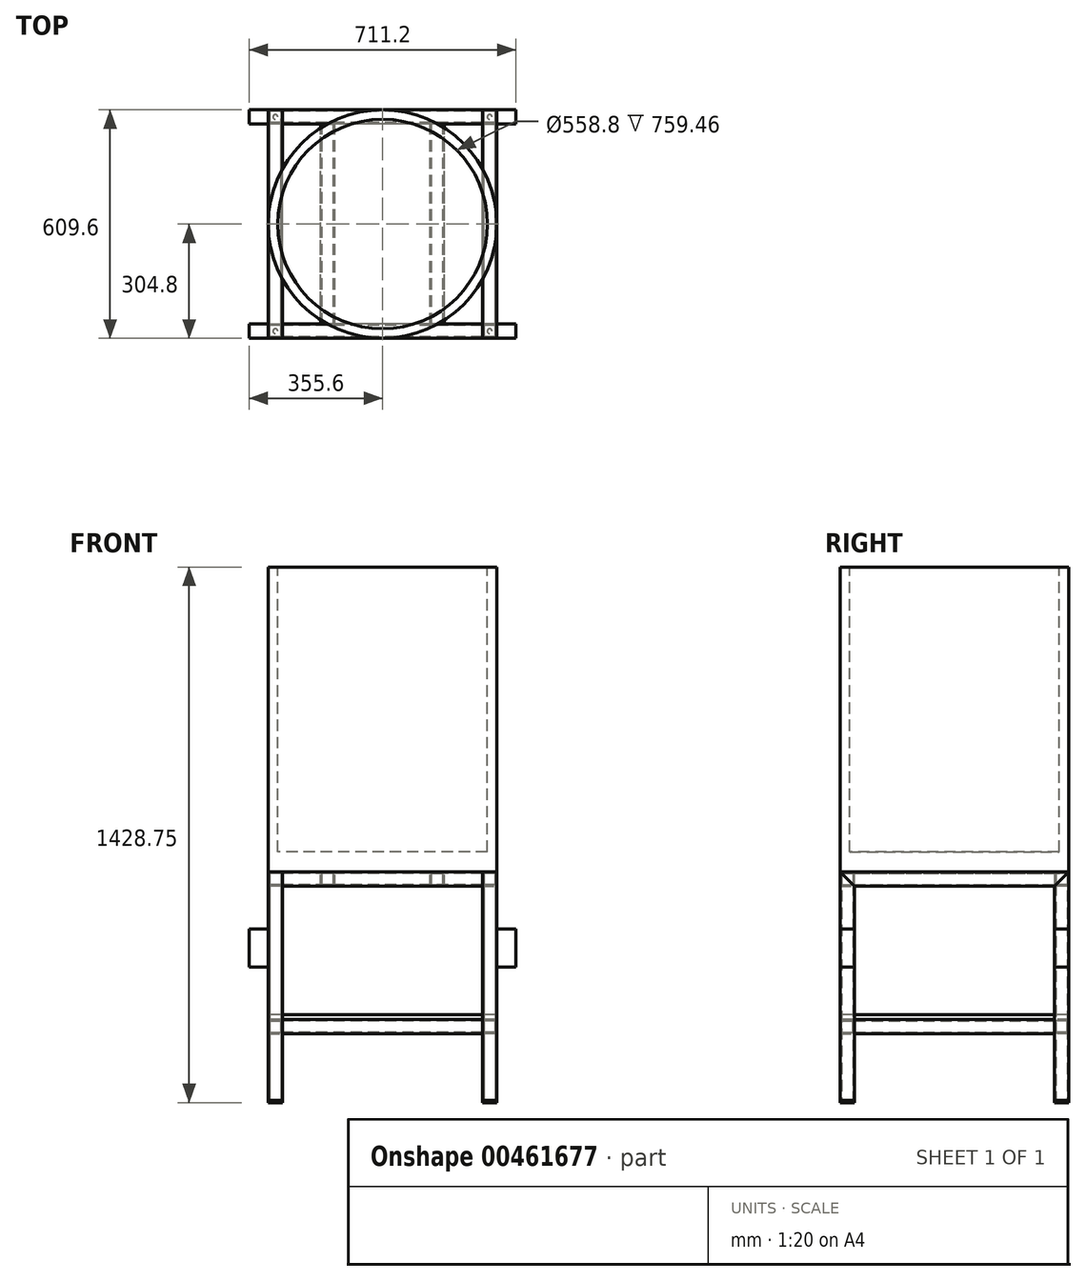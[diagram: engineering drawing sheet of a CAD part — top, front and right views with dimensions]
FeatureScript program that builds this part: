
annotation { "Feature Type Name" : "Feature", "Feature Type Description" : "" }
export const myFeature = defineFeature(function(context is Context, id is Id, definition is map)
    precondition{}
    {
        {
            var Q0;
            Q0=qCreatedBy(makeId("Top.planeOp"),FACE);
            var sketch = newSketch(context, id + "F0", { "sketchPlane" : qUnion([Q0])});
            skCircle(sketch, "E0", {"center": v(0, 0) * mm, "radius": 304.8 * mm});
            skSolve(sketch);
        }
        {
            var Q0;
            Q0=makeQuery(id+"F0.imprint","IMPRINT",FACE,{"disambiguationData":[TD([[makeQuery(id+"F0.imprint","IMPRINT",EDGE,{"derivedFrom":sQuery(id+"F0.wireOp",EDGE,"E0")}),1.0]])]});
            extrude(context, id + "F1", {"entities" : qUnion([Q0]), "depth" : 812.8 * mm});
        }
        {
            var Q0;
            Q0=qCreatedBy(makeId("Front.planeOp"),FACE);
            var sketch = newSketch(context, id + "F2", { "sketchPlane" : qUnion([Q0])});
            skLineSegment(sketch, "E1.bottom", {"start": v(304.8, -38.1) * mm, "end": v(266.7, -38.1) * mm});
            skLineSegment(sketch, "E1.top", {"start": v(304.8, 0) * mm, "end": v(266.7, 0) * mm});
            skLineSegment(sketch, "E1.left", {"start": v(304.8, -38.1) * mm, "end": v(304.8, 0) * mm});
            skLineSegment(sketch, "E1.right", {"start": v(266.7, -38.1) * mm, "end": v(266.7, 0) * mm});
            skPoint(sketch, "E1.middle", {"position": v(285.75, -19.05) * mm});
            skLineSegment(sketch, "E2.0", {"start": v(301, -3.81) * mm, "end": v(270.5, -3.81) * mm});
            skLineSegment(sketch, "E2.1", {"start": v(301, -34.3) * mm, "end": v(301, -3.81) * mm});
            skLineSegment(sketch, "E2.2", {"start": v(301, -34.3) * mm, "end": v(270.5, -34.3) * mm});
            skLineSegment(sketch, "E2.3", {"start": v(270.5, -34.3) * mm, "end": v(270.5, -3.81) * mm});
            skSolve(sketch);
        }
        {
            var Q0;
            Q0 = qSketchRegion(id + "F2", true);
            extrude(context, id + "F3", {"entities" : qUnion([Q0]), "endBound" : BoundingType.SYMMETRIC, "depth" : 609.6 * mm});
        }
        {
            var Q0;
            Q0=makeQuery(id+"F3.opExtrude","SWEPT_FACE",FACE,{"disambiguationData":[OSD([sQuery(id+"F2.wireOp",EDGE,"E1.left")])]});
            var sketch = newSketch(context, id + "F4", { "sketchPlane" : qUnion([Q0])});
            skLineSegment(sketch, "E3", {"start": v(-304.8, 0) * mm, "end": v(-266.7, -38.1) * mm});
            skLineSegment(sketch, "E4", {"start": v(-266.7, -38.1) * mm, "end": v(-266.7, -51.91) * mm});
            skLineSegment(sketch, "E5", {"start": v(-266.7, -51.91) * mm, "end": v(-315.93, -51.91) * mm});
            skLineSegment(sketch, "E6", {"start": v(-315.93, -51.91) * mm, "end": v(-315.93, 0) * mm});
            skLineSegment(sketch, "E7", {"start": v(-315.93, 0) * mm, "end": v(-304.8, 0) * mm});
            skLineSegment(sketch, "E8", {"start": v(0, 0) * mm, "end": v(0, -21.94) * mm, "construction": true});
            skLineSegment(sketch, "E9.MirrorCS", {"start": v(315.93, 0) * mm, "end": v(304.8, 0) * mm});
            skLineSegment(sketch, "E10.MirrorCS", {"start": v(266.7, -38.1) * mm, "end": v(266.7, -51.91) * mm});
            skLineSegment(sketch, "E11.MirrorCS", {"start": v(304.8, 0) * mm, "end": v(266.7, -38.1) * mm});
            skLineSegment(sketch, "E12.MirrorCS", {"start": v(266.7, -51.91) * mm, "end": v(315.93, -51.91) * mm});
            skLineSegment(sketch, "E13.MirrorCS", {"start": v(315.93, -51.91) * mm, "end": v(315.93, 0) * mm});
            skSolve(sketch);
        }
        {
            var Q0;
            Q0 = qSketchRegion(id + "F4", true);
            var Q1;
            Q1=makeQuery(id+"F3.opExtrude","SWEPT_FACE",FACE,{"disambiguationData":[OSD([sQuery(id+"F2.wireOp",EDGE,"E1.right")])]});
            extrude(context, id + "F5", {"entities" : qUnion([Q0]), "operationType" : NewBodyOperationType.REMOVE, "endBound" : BoundingType.UP_TO_SURFACE, "oppositeDirection" : true, "endBoundEntityFace" : qUnion([Q1]), "depth" : 25.4 * mm});
        }
        {
            var Q0;
            Q0=makeQuery(id+"F3.opExtrude","SWEPT_BODY",BODY,{"disambiguationData":[OSD([sQuery(id+"F2.wireOp",EDGE,"E1.bottom"),sQuery(id+"F2.wireOp",EDGE,"E1.top"),sQuery(id+"F2.wireOp",EDGE,"E1.left"),sQuery(id+"F2.wireOp",EDGE,"E1.right"),sQuery(id+"F2.wireOp",EDGE,"E2.0"),sQuery(id+"F2.wireOp",EDGE,"E2.1"),sQuery(id+"F2.wireOp",EDGE,"E2.2"),sQuery(id+"F2.wireOp",EDGE,"E2.3")])]});
            var Q1;
            Q1=qCreatedBy(makeId("Right.planeOp"),FACE);
            mirror(context, id + "F6", {"entities" : qUnion([Q0]), "mirrorPlane" : qUnion([Q1])});
        }
        {
            var Q0;
            Q0=qCreatedBy(makeId("Top.planeOp"),FACE);
            cPlane(context, id + "F7", {"entities" : qUnion([Q0]), "cplaneType" : CPlaneType.OFFSET, "offset" : 609.6 * mm, "oppositeDirection" : true, "width" : 152.4 * mm, "height" : 152.4 * mm});
        }
        {
            var Q0;
            Q0=qCreatedBy(id+"F7.planeOp",FACE);
            var sketch = newSketch(context, id + "F8", { "sketchPlane" : qUnion([Q0])});
            skLineSegment(sketch, "E14.bottom", {"start": v(304.8, -266.7) * mm, "end": v(266.7, -266.7) * mm});
            skLineSegment(sketch, "E14.top", {"start": v(304.8, -304.8) * mm, "end": v(266.7, -304.8) * mm});
            skLineSegment(sketch, "E14.left", {"start": v(304.8, -266.7) * mm, "end": v(304.8, -304.8) * mm});
            skLineSegment(sketch, "E14.right", {"start": v(266.7, -266.7) * mm, "end": v(266.7, -304.8) * mm});
            skPoint(sketch, "E14.middle", {"position": v(285.75, -285.75) * mm});
            skLineSegment(sketch, "E15.0", {"start": v(270.5, -270.51) * mm, "end": v(270.5, -301) * mm});
            skLineSegment(sketch, "E15.1", {"start": v(300.99, -270.51) * mm, "end": v(270.5, -270.51) * mm});
            skLineSegment(sketch, "E15.2", {"start": v(300.99, -270.51) * mm, "end": v(300.99, -301) * mm});
            skLineSegment(sketch, "E15.3", {"start": v(300.99, -301) * mm, "end": v(270.5, -301) * mm});
            skSolve(sketch);
        }
        {
            var Q0;
            Q0 = qSketchRegion(id + "F8", true);
            var Q1;
            Q1=makeQuery(id+"F5.boolean.opBoolean","COPY",FACE,{"derivedFrom":makeQuery(id+"F5.opExtrude","SWEPT_FACE",FACE,{"disambiguationData":[OSD([sQuery(id+"F4.wireOp",EDGE,"E3")])]})});
            extrude(context, id + "F9", {"entities" : qUnion([Q0]), "endBound" : BoundingType.UP_TO_SURFACE, "endBoundEntityFace" : qUnion([Q1]), "depth" : 345.44 * mm});
        }
        {
            var Q0;
            Q0=makeQuery(id+"F9.opExtrude","SWEPT_BODY",BODY,{"disambiguationData":[OSD([sQuery(id+"F8.wireOp",EDGE,"E14.bottom"),sQuery(id+"F8.wireOp",EDGE,"E14.top"),sQuery(id+"F8.wireOp",EDGE,"E14.left"),sQuery(id+"F8.wireOp",EDGE,"E14.right"),sQuery(id+"F8.wireOp",EDGE,"E15.0"),sQuery(id+"F8.wireOp",EDGE,"E15.1"),sQuery(id+"F8.wireOp",EDGE,"E15.2"),sQuery(id+"F8.wireOp",EDGE,"E15.3")])]});
            var Q1;
            Q1=qCreatedBy(makeId("Front.planeOp"),FACE);
            mirror(context, id + "F10", {"entities" : qUnion([Q0]), "mirrorPlane" : qUnion([Q1])});
        }
        {
            var Q0;
            Q0=makeQuery(id+"F9.opExtrude","SWEPT_BODY",BODY,{"disambiguationData":[OSD([sQuery(id+"F8.wireOp",EDGE,"E14.bottom"),sQuery(id+"F8.wireOp",EDGE,"E14.top"),sQuery(id+"F8.wireOp",EDGE,"E14.left"),sQuery(id+"F8.wireOp",EDGE,"E14.right"),sQuery(id+"F8.wireOp",EDGE,"E15.0"),sQuery(id+"F8.wireOp",EDGE,"E15.1"),sQuery(id+"F8.wireOp",EDGE,"E15.2"),sQuery(id+"F8.wireOp",EDGE,"E15.3")])]});
            var Q1;
            Q1=makeQuery(id+"F10.opPattern","COPY",BODY,{"derivedFrom":makeQuery(id+"F9.opExtrude","SWEPT_BODY",BODY,{"disambiguationData":[OSD([sQuery(id+"F8.wireOp",EDGE,"E14.bottom"),sQuery(id+"F8.wireOp",EDGE,"E14.top"),sQuery(id+"F8.wireOp",EDGE,"E14.left"),sQuery(id+"F8.wireOp",EDGE,"E14.right"),sQuery(id+"F8.wireOp",EDGE,"E15.0"),sQuery(id+"F8.wireOp",EDGE,"E15.1"),sQuery(id+"F8.wireOp",EDGE,"E15.2"),sQuery(id+"F8.wireOp",EDGE,"E15.3")])]}),"instanceName":"1"});
            var Q2;
            Q2=qCreatedBy(makeId("Right.planeOp"),FACE);
            mirror(context, id + "F11", {"entities" : qUnion([Q0, Q1]), "mirrorPlane" : qUnion([Q2])});
        }
        {
            var Q0;
            Q0=qCreatedBy(makeId("Right.planeOp"),FACE);
            var sketch = newSketch(context, id + "F12", { "sketchPlane" : qUnion([Q0])});
            skLineSegment(sketch, "E16.bottom", {"start": v(-266.7, -38.1) * mm, "end": v(-304.8, -38.1) * mm});
            skLineSegment(sketch, "E16.top", {"start": v(-266.7, 0) * mm, "end": v(-304.8, 0) * mm});
            skLineSegment(sketch, "E16.left", {"start": v(-266.7, -38.1) * mm, "end": v(-266.7, 0) * mm});
            skLineSegment(sketch, "E16.right", {"start": v(-304.8, -38.1) * mm, "end": v(-304.8, 0) * mm});
            skPoint(sketch, "E16.middle", {"position": v(-285.75, -19.05) * mm});
            skLineSegment(sketch, "E17.0", {"start": v(-270.51, -3.81) * mm, "end": v(-301, -3.81) * mm});
            skLineSegment(sketch, "E17.1", {"start": v(-270.51, -34.29) * mm, "end": v(-270.51, -3.81) * mm});
            skLineSegment(sketch, "E17.2", {"start": v(-270.51, -34.29) * mm, "end": v(-301, -34.29) * mm});
            skLineSegment(sketch, "E17.3", {"start": v(-301, -34.29) * mm, "end": v(-301, -3.81) * mm});
            skSolve(sketch);
        }
        {
            var Q0;
            Q0 = qSketchRegion(id + "F12", true);
            var Q1;
            Q1=makeQuery(id+"F3.opExtrude","SWEPT_FACE",FACE,{"disambiguationData":[OSD([sQuery(id+"F2.wireOp",EDGE,"E1.right")])]});
            var Q2;
            Q2=makeQuery(id+"F6.opPattern","COPY",FACE,{"derivedFrom":makeQuery(id+"F3.opExtrude","SWEPT_FACE",FACE,{"disambiguationData":[OSD([sQuery(id+"F2.wireOp",EDGE,"E1.right")])]}),"instanceName":"1"});
            extrude(context, id + "F13", {"entities" : qUnion([Q0]), "endBound" : BoundingType.UP_TO_SURFACE, "endBoundEntityFace" : qUnion([Q1]), "depth" : 533.4 * mm, "hasSecondDirection" : true, "secondDirectionBound" : SecondDirectionBoundingType.UP_TO_SURFACE, "secondDirectionOppositeDirection" : true, "secondDirectionBoundEntityFace" : qUnion([Q2]), "secondDirectionDepth" : 25.4 * mm});
        }
        {
            var Q0;
            Q0=makeQuery(id+"F13.opExtrude","SWEPT_BODY",BODY,{"disambiguationData":[OSD([sQuery(id+"F12.wireOp",EDGE,"E16.bottom"),sQuery(id+"F12.wireOp",EDGE,"E16.top"),sQuery(id+"F12.wireOp",EDGE,"E16.left"),sQuery(id+"F12.wireOp",EDGE,"E16.right"),sQuery(id+"F12.wireOp",EDGE,"E17.0"),sQuery(id+"F12.wireOp",EDGE,"E17.1"),sQuery(id+"F12.wireOp",EDGE,"E17.2"),sQuery(id+"F12.wireOp",EDGE,"E17.3")])]});
            var Q1;
            Q1=qCreatedBy(makeId("Front.planeOp"),FACE);
            mirror(context, id + "F14", {"entities" : qUnion([Q0]), "mirrorPlane" : qUnion([Q1])});
        }
        {
            var Q0;
            Q0=makeQuery(id+"F13.opExtrude","SWEPT_FACE",FACE,{"disambiguationData":[OSD([sQuery(id+"F12.wireOp",EDGE,"E16.bottom")])]});
            cPlane(context, id + "F15", {"entities" : qUnion([Q0]), "cplaneType" : CPlaneType.OFFSET, "offset" : 177.8 * mm, "width" : 152.4 * mm, "height" : 152.4 * mm});
        }
        {
            var Q0;
            Q0=makeQuery(id+"F13.opExtrude","SWEPT_BODY",BODY,{"disambiguationData":[OSD([sQuery(id+"F12.wireOp",EDGE,"E16.bottom"),sQuery(id+"F12.wireOp",EDGE,"E16.top"),sQuery(id+"F12.wireOp",EDGE,"E16.left"),sQuery(id+"F12.wireOp",EDGE,"E16.right"),sQuery(id+"F12.wireOp",EDGE,"E17.0"),sQuery(id+"F12.wireOp",EDGE,"E17.1"),sQuery(id+"F12.wireOp",EDGE,"E17.2"),sQuery(id+"F12.wireOp",EDGE,"E17.3")])]});
            var Q1;
            Q1=makeQuery(id+"F14.opPattern","COPY",BODY,{"derivedFrom":makeQuery(id+"F13.opExtrude","SWEPT_BODY",BODY,{"disambiguationData":[OSD([sQuery(id+"F12.wireOp",EDGE,"E16.bottom"),sQuery(id+"F12.wireOp",EDGE,"E16.top"),sQuery(id+"F12.wireOp",EDGE,"E16.left"),sQuery(id+"F12.wireOp",EDGE,"E16.right"),sQuery(id+"F12.wireOp",EDGE,"E17.0"),sQuery(id+"F12.wireOp",EDGE,"E17.1"),sQuery(id+"F12.wireOp",EDGE,"E17.2"),sQuery(id+"F12.wireOp",EDGE,"E17.3")])]}),"instanceName":"1"});
            var Q2;
            Q2=qCreatedBy(id+"F15.planeOp",FACE);
            mirror(context, id + "F16", {"entities" : qUnion([Q0, Q1]), "mirrorPlane" : qUnion([Q2])});
        }
        {
            var Q0;
            Q0=qCreatedBy(makeId("Front.planeOp"),FACE);
            var sketch = newSketch(context, id + "F17", { "sketchPlane" : qUnion([Q0])});
            skLineSegment(sketch, "E18.bottom", {"start": v(304.8, -431.8) * mm, "end": v(266.7, -431.8) * mm});
            skLineSegment(sketch, "E18.top", {"start": v(304.8, -393.7) * mm, "end": v(266.7, -393.7) * mm});
            skLineSegment(sketch, "E18.left", {"start": v(304.8, -431.8) * mm, "end": v(304.8, -393.7) * mm});
            skLineSegment(sketch, "E18.right", {"start": v(266.7, -431.8) * mm, "end": v(266.7, -393.7) * mm});
            skPoint(sketch, "E18.middle", {"position": v(285.75, -412.75) * mm});
            skLineSegment(sketch, "E19.0", {"start": v(300.99, -397.5) * mm, "end": v(270.5, -397.5) * mm});
            skLineSegment(sketch, "E19.1", {"start": v(300.99, -427.99) * mm, "end": v(300.99, -397.5) * mm});
            skLineSegment(sketch, "E19.2", {"start": v(300.99, -427.99) * mm, "end": v(270.5, -427.99) * mm});
            skLineSegment(sketch, "E19.3", {"start": v(270.5, -427.99) * mm, "end": v(270.5, -397.5) * mm});
            skSolve(sketch);
        }
        {
            var Q0;
            Q0 = qSketchRegion(id + "F17", true);
            extrude(context, id + "F18", {"entities" : qUnion([Q0]), "endBound" : BoundingType.UP_TO_NEXT, "depth" : 25.4 * mm, "hasSecondDirection" : true, "secondDirectionBound" : SecondDirectionBoundingType.UP_TO_NEXT, "secondDirectionOppositeDirection" : true, "secondDirectionDepth" : 25.4 * mm});
        }
        {
            var Q0;
            Q0=makeQuery(id+"F18.opExtrude","SWEPT_BODY",BODY,{"disambiguationData":[OSD([sQuery(id+"F17.wireOp",EDGE,"E18.bottom"),sQuery(id+"F17.wireOp",EDGE,"E18.top"),sQuery(id+"F17.wireOp",EDGE,"E18.left"),sQuery(id+"F17.wireOp",EDGE,"E18.right"),sQuery(id+"F17.wireOp",EDGE,"E19.0"),sQuery(id+"F17.wireOp",EDGE,"E19.1"),sQuery(id+"F17.wireOp",EDGE,"E19.2"),sQuery(id+"F17.wireOp",EDGE,"E19.3")])]});
            var Q1;
            Q1=qCreatedBy(makeId("Right.planeOp"),FACE);
            mirror(context, id + "F19", {"entities" : qUnion([Q0]), "mirrorPlane" : qUnion([Q1])});
        }
        {
            var Q0;
            Q0=qCreatedBy(makeId("Front.planeOp"),FACE);
            var sketch = newSketch(context, id + "F20", { "sketchPlane" : qUnion([Q0])});
            skLineSegment(sketch, "E20.bottom", {"start": v(-127, -38.1) * mm, "end": v(-165.1, -38.1) * mm});
            skLineSegment(sketch, "E20.top", {"start": v(-127, 0) * mm, "end": v(-165.1, 0) * mm});
            skLineSegment(sketch, "E20.left", {"start": v(-127, -38.1) * mm, "end": v(-127, 0) * mm});
            skLineSegment(sketch, "E20.right", {"start": v(-165.1, -38.1) * mm, "end": v(-165.1, 0) * mm});
            skPoint(sketch, "E20.middle", {"position": v(-146.05, -19.05) * mm});
            skLineSegment(sketch, "E21.0", {"start": v(-130.81, -3.8) * mm, "end": v(-161.29, -3.81) * mm});
            skLineSegment(sketch, "E21.1", {"start": v(-130.81, -34.29) * mm, "end": v(-130.81, -3.8) * mm});
            skLineSegment(sketch, "E21.2", {"start": v(-130.81, -34.29) * mm, "end": v(-161.29, -34.29) * mm});
            skLineSegment(sketch, "E21.3", {"start": v(-161.29, -34.29) * mm, "end": v(-161.29, -3.81) * mm});
            skSolve(sketch);
        }
        {
            var Q0;
            Q0 = qSketchRegion(id + "F20", true);
            extrude(context, id + "F21", {"entities" : qUnion([Q0]), "endBound" : BoundingType.UP_TO_NEXT, "depth" : 25.4 * mm, "hasSecondDirection" : true, "secondDirectionBound" : SecondDirectionBoundingType.UP_TO_NEXT, "secondDirectionOppositeDirection" : true, "secondDirectionDepth" : 25.4 * mm});
        }
        {
            var Q0;
            Q0=makeQuery(id+"F21.opExtrude","SWEPT_BODY",BODY,{"disambiguationData":[OSD([sQuery(id+"F20.wireOp",EDGE,"E20.bottom"),sQuery(id+"F20.wireOp",EDGE,"E20.top"),sQuery(id+"F20.wireOp",EDGE,"E20.left"),sQuery(id+"F20.wireOp",EDGE,"E20.right"),sQuery(id+"F20.wireOp",EDGE,"E21.0"),sQuery(id+"F20.wireOp",EDGE,"E21.1"),sQuery(id+"F20.wireOp",EDGE,"E21.2"),sQuery(id+"F20.wireOp",EDGE,"E21.3")])]});
            var Q1;
            Q1=qCreatedBy(makeId("Right.planeOp"),FACE);
            mirror(context, id + "F22", {"entities" : qUnion([Q0]), "mirrorPlane" : qUnion([Q1])});
        }
        {
            var Q0;
            Q0=makeQuery(id+"F19.opPattern","COPY",FACE,{"derivedFrom":makeQuery(id+"F18.opExtrude","SWEPT_FACE",FACE,{"disambiguationData":[OSD([sQuery(id+"F17.wireOp",EDGE,"E18.top")])]}),"instanceName":"1"});
            var sketch = newSketch(context, id + "F23", { "sketchPlane" : qUnion([Q0])});
            skLineSegment(sketch, "E22.0", {"start": v(266.7, -304.8) * mm, "end": v(-266.7, -304.8) * mm});
            skLineSegment(sketch, "E23.0", {"start": v(266.7, 304.8) * mm, "end": v(-266.7, 304.8) * mm});
            skLineSegment(sketch, "E24", {"start": v(-266.7, 304.8) * mm, "end": v(-266.7, 266.7) * mm});
            skLineSegment(sketch, "E25", {"start": v(-266.7, 266.7) * mm, "end": v(-304.8, 266.7) * mm});
            skLineSegment(sketch, "E26", {"start": v(-304.8, 266.7) * mm, "end": v(-304.8, -266.7) * mm});
            skLineSegment(sketch, "E27", {"start": v(-304.8, -266.7) * mm, "end": v(-266.7, -266.7) * mm});
            skLineSegment(sketch, "E28", {"start": v(-266.7, -266.7) * mm, "end": v(-266.7, -304.8) * mm});
            skLineSegment(sketch, "E29", {"start": v(0, 0) * mm, "end": v(0, 69.38) * mm, "construction": true});
            skLineSegment(sketch, "E30", {"start": v(0, 0) * mm, "end": v(64.68, 0) * mm, "construction": true});
            skLineSegment(sketch, "E31.MirrorCS", {"start": v(304.8, 266.7) * mm, "end": v(304.8, -266.7) * mm});
            skLineSegment(sketch, "E32.MirrorCS", {"start": v(266.7, 266.7) * mm, "end": v(304.8, 266.7) * mm});
            skLineSegment(sketch, "E33.MirrorCS", {"start": v(304.8, -266.7) * mm, "end": v(266.7, -266.7) * mm});
            skLineSegment(sketch, "E34", {"start": v(266.7, -304.8) * mm, "end": v(266.7, -266.7) * mm});
            skLineSegment(sketch, "E35", {"start": v(266.7, 304.8) * mm, "end": v(266.7, 266.7) * mm});
            skSolve(sketch);
        }
        {
            var Q0;
            Q0 = qSketchRegion(id + "F23", true);
            extrude(context, id + "F24", {"entities" : qUnion([Q0]), "depth" : 12.7 * mm});
        }
        {
            var Q0;
            Q0=qCreatedBy(id+"F7.planeOp",FACE);
            var sketch = newSketch(context, id + "F25", { "sketchPlane" : qUnion([Q0])});
            skLineSegment(sketch, "E36.bottom", {"start": v(304.8, -304.8) * mm, "end": v(266.7, -304.8) * mm});
            skLineSegment(sketch, "E36.top", {"start": v(304.8, -266.7) * mm, "end": v(266.7, -266.7) * mm});
            skLineSegment(sketch, "E36.left", {"start": v(304.8, -304.8) * mm, "end": v(304.8, -266.7) * mm});
            skLineSegment(sketch, "E36.right", {"start": v(266.7, -304.8) * mm, "end": v(266.7, -266.7) * mm});
            skLineSegment(sketch, "E37", {"start": v(266.7, -304.8) * mm, "end": v(304.8, -266.7) * mm, "construction": true});
            skLineSegment(sketch, "E38", {"start": v(304.8, -304.8) * mm, "end": v(266.7, -266.7) * mm, "construction": true});
            skCircle(sketch, "E39", {"center": v(285.75, -285.75) * mm, "radius": 6.35 * mm});
            skSolve(sketch);
        }
        {
            var Q0;
            Q0 = qSketchRegion(id + "F25", true);
            extrude(context, id + "F26", {"entities" : qUnion([Q0]), "oppositeDirection" : true, "depth" : 6.35 * mm});
        }
        {
            var Q0;
            Q0=makeQuery(id+"F26.opExtrude","SWEPT_BODY",BODY,{"disambiguationData":[OSD([sQuery(id+"F25.wireOp",EDGE,"E36.bottom"),sQuery(id+"F25.wireOp",EDGE,"E36.top"),sQuery(id+"F25.wireOp",EDGE,"E36.left"),sQuery(id+"F25.wireOp",EDGE,"E36.right"),sQuery(id+"F25.wireOp",EDGE,"E39")])]});
            var Q1;
            Q1=qCreatedBy(makeId("Right.planeOp"),FACE);
            mirror(context, id + "F27", {"entities" : qUnion([Q0]), "mirrorPlane" : qUnion([Q1])});
        }
        {
            var Q0;
            Q0=makeQuery(id+"F26.opExtrude","SWEPT_BODY",BODY,{"disambiguationData":[OSD([sQuery(id+"F25.wireOp",EDGE,"E36.bottom"),sQuery(id+"F25.wireOp",EDGE,"E36.top"),sQuery(id+"F25.wireOp",EDGE,"E36.left"),sQuery(id+"F25.wireOp",EDGE,"E36.right"),sQuery(id+"F25.wireOp",EDGE,"E39")])]});
            var Q1;
            Q1=makeQuery(id+"F27.opPattern","COPY",BODY,{"derivedFrom":makeQuery(id+"F26.opExtrude","SWEPT_BODY",BODY,{"disambiguationData":[OSD([sQuery(id+"F25.wireOp",EDGE,"E36.bottom"),sQuery(id+"F25.wireOp",EDGE,"E36.top"),sQuery(id+"F25.wireOp",EDGE,"E36.left"),sQuery(id+"F25.wireOp",EDGE,"E36.right"),sQuery(id+"F25.wireOp",EDGE,"E39")])]}),"instanceName":"1"});
            var Q2;
            Q2=qCreatedBy(makeId("Front.planeOp"),FACE);
            mirror(context, id + "F28", {"entities" : qUnion([Q0, Q1]), "mirrorPlane" : qUnion([Q2])});
        }
        {
            var Q0;
            Q0=makeQuery(id+"F1.opExtrude","CAP_FACE",FACE,{"disambiguationData":[OSD([sQuery(id+"F0.wireOp",EDGE,"E0")])],"isStart":false});
            var sketch = newSketch(context, id + "F29", { "sketchPlane" : qUnion([Q0])});
            skCircle(sketch, "E40", {"center": v(0, 0) * mm, "radius": 279.4 * mm});
            skSolve(sketch);
        }
        {
            var Q0;
            Q0 = qSketchRegion(id + "F29", true);
            extrude(context, id + "F30", {"entities" : qUnion([Q0]), "operationType" : NewBodyOperationType.REMOVE, "oppositeDirection" : true, "depth" : 759.46 * mm});
        }
        {
            var Q0;
            Q0=makeQuery(id+"F11.opPattern","COPY",FACE,{"derivedFrom":makeQuery(id+"F9.opExtrude","SWEPT_FACE",FACE,{"disambiguationData":[OSD([sQuery(id+"F8.wireOp",EDGE,"E14.left")])]}),"instanceName":"1"});
            var sketch = newSketch(context, id + "F31", { "sketchPlane" : qUnion([Q0])});
            skLineSegment(sketch, "E41.bottom", {"start": v(-304.8, -152.4) * mm, "end": v(-266.7, -152.4) * mm});
            skLineSegment(sketch, "E41.top", {"start": v(-304.8, -254) * mm, "end": v(-266.7, -254) * mm});
            skLineSegment(sketch, "E41.left", {"start": v(-304.8, -152.4) * mm, "end": v(-304.8, -254) * mm});
            skLineSegment(sketch, "E41.right", {"start": v(-266.7, -152.4) * mm, "end": v(-266.7, -254) * mm});
            skLineSegment(sketch, "E42", {"start": v(0, 0) * mm, "end": v(0, -69.92) * mm, "construction": true});
            skLineSegment(sketch, "E43.MirrorCS", {"start": v(304.8, -254) * mm, "end": v(266.7, -254) * mm});
            skLineSegment(sketch, "E44.MirrorCS", {"start": v(304.8, -152.4) * mm, "end": v(266.7, -152.4) * mm});
            skLineSegment(sketch, "E45.MirrorCS", {"start": v(266.7, -152.4) * mm, "end": v(266.7, -254) * mm});
            skLineSegment(sketch, "E46.MirrorCS", {"start": v(304.8, -152.4) * mm, "end": v(304.8, -254) * mm});
            skSolve(sketch);
        }
        {
            var Q0;
            Q0 = qSketchRegion(id + "F31", true);
            extrude(context, id + "F32", {"entities" : qUnion([Q0]), "depth" : 50.8 * mm});
        }
        {
            var Q0;
            Q0=makeQuery(id+"F32.opExtrude","SWEPT_BODY",BODY,{"disambiguationData":[OSD([sQuery(id+"F31.wireOp",EDGE,"E43.MirrorCS"),sQuery(id+"F31.wireOp",EDGE,"E44.MirrorCS"),sQuery(id+"F31.wireOp",EDGE,"E45.MirrorCS"),sQuery(id+"F31.wireOp",EDGE,"E46.MirrorCS")])]});
            var Q1;
            Q1=makeQuery(id+"F32.opExtrude","SWEPT_BODY",BODY,{"disambiguationData":[OSD([sQuery(id+"F31.wireOp",EDGE,"E41.bottom"),sQuery(id+"F31.wireOp",EDGE,"E41.top"),sQuery(id+"F31.wireOp",EDGE,"E41.left"),sQuery(id+"F31.wireOp",EDGE,"E41.right")])]});
            var Q2;
            Q2=qCreatedBy(makeId("Right.planeOp"),FACE);
            mirror(context, id + "F33", {"entities" : qUnion([Q0, Q1]), "mirrorPlane" : qUnion([Q2])});
        }
    });
